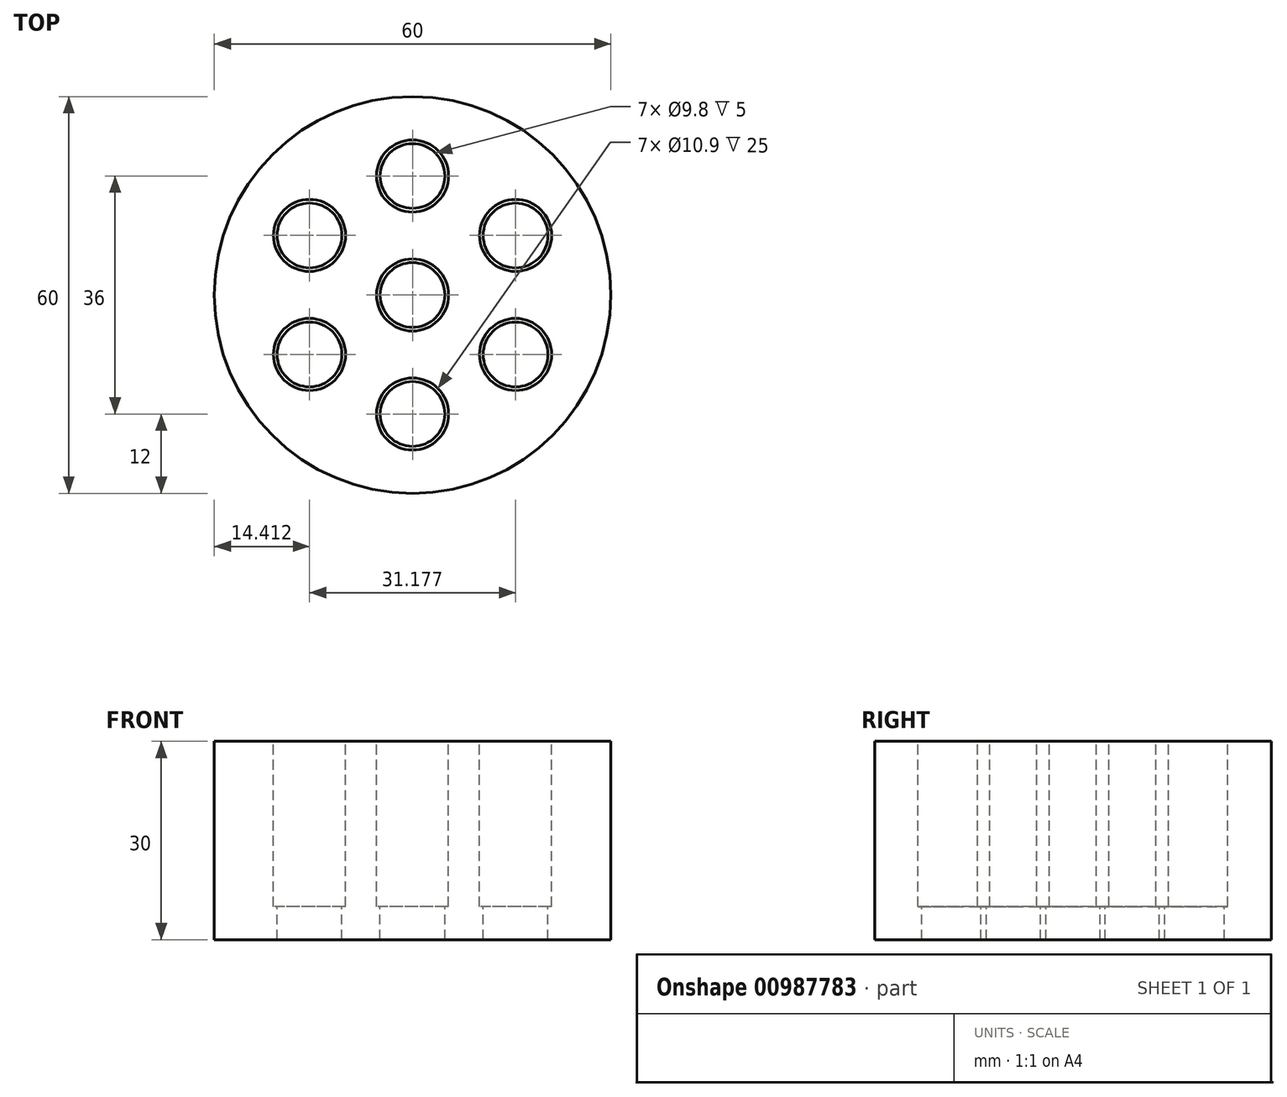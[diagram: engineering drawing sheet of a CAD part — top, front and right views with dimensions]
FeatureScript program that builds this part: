
annotation { "Feature Type Name" : "Feature", "Feature Type Description" : "" }
export const myFeature = defineFeature(function(context is Context, id is Id, definition is map)
    precondition{}
    {
        {
            var Q0;
            Q0=qCreatedBy(makeId("Top.planeOp"),FACE);
            var sketch = newSketch(context, id + "F0", { "sketchPlane" : qUnion([Q0])});
            skCircle(sketch, "E0", {"center": v(0, 0) * mm, "radius": 30 * mm});
            skSolve(sketch);
        }
        {
            var Q0;
            Q0 = qSketchRegion(id + "F0", true);
            extrude(context, id + "F1", {"entities" : qUnion([Q0]), "depth" : 30 * mm, "offsetDistance" : 25 * mm});
        }
        {
            var Q0;
            Q0=makeQuery(id+"F1.opExtrude","CAP_FACE",FACE,{"disambiguationData":[OSD([sQuery(id+"F0.wireOp",EDGE,"E0")])],"isStart":false});
            var sketch = newSketch(context, id + "F2", { "sketchPlane" : qUnion([Q0])});
            skCircle(sketch, "E1", {"center": v(0, 0) * mm, "radius": 4.9 * mm});
            skCircle(sketch, "E2", {"center": v(0, 18) * mm, "radius": 4.9 * mm});
            skCircle(sketch, "E3.1.0", {"center": v(-15.59, 9) * mm, "radius": 4.9 * mm});
            skCircle(sketch, "E3.2.0", {"center": v(-15.59, -9) * mm, "radius": 4.9 * mm});
            skCircle(sketch, "E3.3.0", {"center": v(0, -18) * mm, "radius": 4.9 * mm});
            skCircle(sketch, "E3.4.0", {"center": v(15.59, -9) * mm, "radius": 4.9 * mm});
            skCircle(sketch, "E3.5.0", {"center": v(15.59, 9) * mm, "radius": 4.9 * mm});
            skSolve(sketch);
        }
        {
            var Q0;
            Q0 = qSketchRegion(id + "F2", true);
            var Q1;
            Q1=makeQuery(id+"F1.opExtrude","CAP_FACE",FACE,{"disambiguationData":[OSD([sQuery(id+"F0.wireOp",EDGE,"E0")])],"isStart":true});
            extrude(context, id + "F3", {"entities" : qUnion([Q0]), "operationType" : NewBodyOperationType.REMOVE, "endBound" : BoundingType.UP_TO_SURFACE, "oppositeDirection" : true, "depth" : 25 * mm, "endBoundEntityFace" : qUnion([Q1]), "offsetDistance" : 25 * mm});
        }
        {
            var Q0;
            Q0=makeQuery(id+"F1.opExtrude","CAP_FACE",FACE,{"disambiguationData":[OSD([sQuery(id+"F0.wireOp",EDGE,"E0")])],"isStart":false});
            var sketch = newSketch(context, id + "F4", { "sketchPlane" : qUnion([Q0])});
            skCircle(sketch, "E4", {"center": v(0, 0) * mm, "radius": 5.45 * mm});
            skCircle(sketch, "E5", {"center": v(0, 18) * mm, "radius": 5.45 * mm});
            skCircle(sketch, "E6", {"center": v(-15.59, 9) * mm, "radius": 5.45 * mm});
            skCircle(sketch, "E7", {"center": v(-15.59, -9) * mm, "radius": 5.45 * mm});
            skCircle(sketch, "E8", {"center": v(0, -18) * mm, "radius": 5.45 * mm});
            skCircle(sketch, "E9", {"center": v(15.59, -9) * mm, "radius": 5.45 * mm});
            skCircle(sketch, "E10", {"center": v(15.59, 9) * mm, "radius": 5.45 * mm});
            skSolve(sketch);
        }
        {
            var Q0;
            Q0 = qSketchRegion(id + "F4", true);
            extrude(context, id + "F5", {"entities" : qUnion([Q0]), "operationType" : NewBodyOperationType.REMOVE, "oppositeDirection" : true, "depth" : 25 * mm, "offsetDistance" : 25 * mm});
        }
    });
